AUTODESK INVENTOR PART (.ipt)
format: ipt  version: 2022 (Build 260153000, 153)  size: 181,248 bytes
history: native  units: mm
features: sketch x5, extrude x4, other x4, projected_geometry x3, boolean_combine x2, plane x2, mirror x2, shell x1
ambient origin geometry x8: Origin, YZ Plane, XZ Plane, XY Plane, X Axis, Y Axis, Z Axis, Center Point
bodies: Solid3 (feature_tree), Solid4 (feature_tree)
feature tree (23):
  extrude  "Extrusion3"  Depth=292.1mm
  sketch  "Sketch2"  dims[d15=88.9mm d16=88.9mm]
  shell  "Shell1"  Thickness=31.75mm
  sketch  "Sketch3"  dims[d17=6.35mm d20=25.4mm]
  other  "Work Axis3"
  other  "Work Axis4"
  other  "Work Axis5"
  other  "Work Axis6"
  sketch  "Sketch6"  dims[d24=25.4mm d25=7.271042mm d26=6.35mm d27=0.0mm d28=6.5mm d42=10.0mm d43=0.0mm d44=10.0mm d45=0.0mm]
  extrude  "Extrusion6"  Depth=88.9mm
  extrude  "Extrusion7"  Depth=25.4mm
  boolean_combine  "Combine1"
  boolean_combine  "Combine2"
  extrude  "Extrusion4"  Depth=88.9mm
  plane  "Work Plane1"
  plane  "Work Plane2"
  mirror  "Mirror1"
  mirror  "Mirror2"
  sketch  "Sketch1"  dims[d11=292.1mm d12=292.1mm d13=31.75mm d14=0.0mm]
  projected_geometry  "Projected Loop1"
  sketch  "Sketch4"  dims[d22=88.9mm d23=88.9mm]
  projected_geometry  "Projected Loop2"
  projected_geometry  "Projected Loop3"
